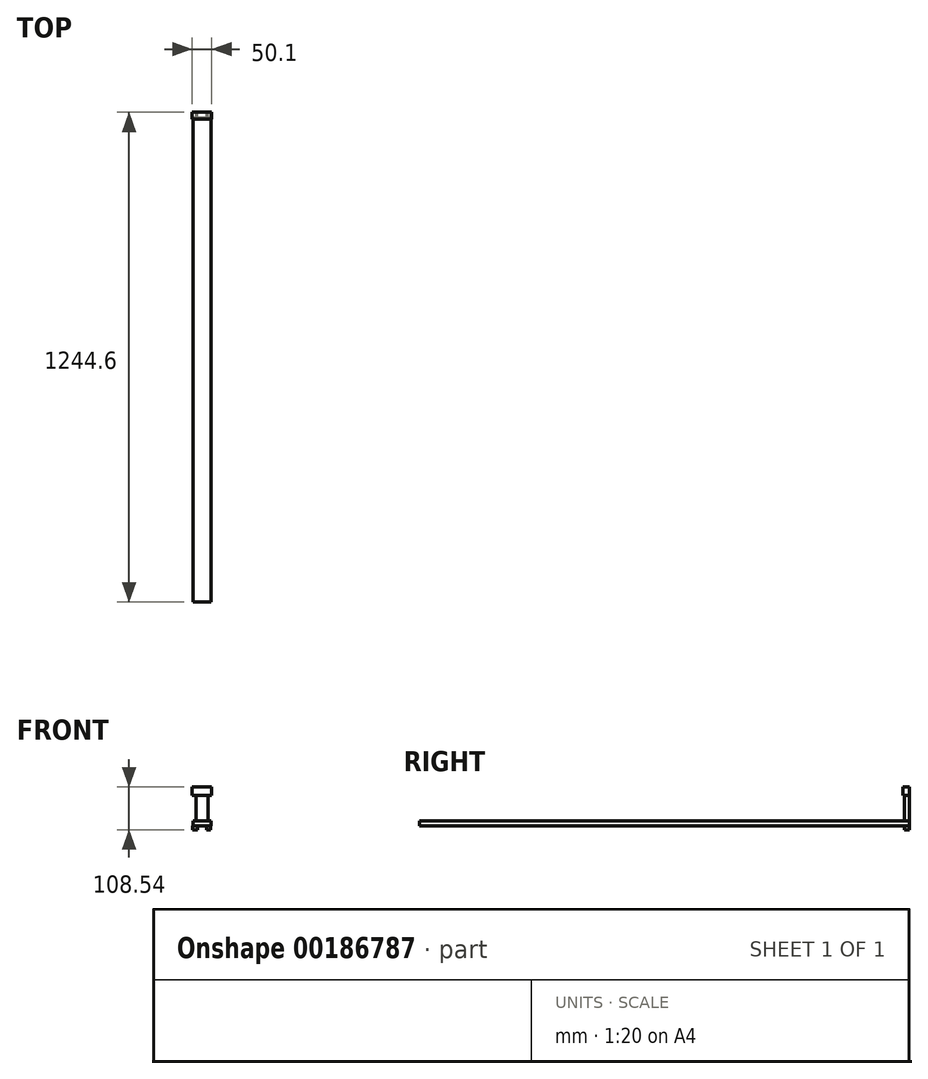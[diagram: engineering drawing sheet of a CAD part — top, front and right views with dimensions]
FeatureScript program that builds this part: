
annotation { "Feature Type Name" : "Feature", "Feature Type Description" : "" }
export const myFeature = defineFeature(function(context is Context, id is Id, definition is map)
    precondition{}
    {
        {
            var Q0;
            Q0=qCreatedBy(makeId("Front.planeOp"),FACE);
            var sketch = newSketch(context, id + "F0", { "sketchPlane" : qUnion([Q0])});
            skLineSegment(sketch, "E0.bottom", {"start": v(-11.69, 50.51) * mm, "end": v(18.65, 50.51) * mm});
            skLineSegment(sketch, "E0.top", {"start": v(-11.69, -14.33) * mm, "end": v(18.65, -14.33) * mm});
            skLineSegment(sketch, "E0.left", {"start": v(-11.69, 50.51) * mm, "end": v(-11.69, -14.33) * mm});
            skLineSegment(sketch, "E0.right", {"start": v(18.65, 50.51) * mm, "end": v(18.65, -14.33) * mm});
            skSolve(sketch);
        }
        {
            var Q0;
            Q0=qCreatedBy(makeId("Front.planeOp"),FACE);
            var sketch = newSketch(context, id + "F1", { "sketchPlane" : qUnion([Q0])});
            skLineSegment(sketch, "E1.bottom", {"start": v(-21.7, 72.22) * mm, "end": v(28.39, 72.22) * mm});
            skLineSegment(sketch, "E1.top", {"start": v(-21.7, 50.79) * mm, "end": v(28.39, 50.79) * mm});
            skLineSegment(sketch, "E1.left", {"start": v(-21.7, 72.22) * mm, "end": v(-21.7, 50.79) * mm});
            skLineSegment(sketch, "E1.right", {"start": v(28.39, 72.22) * mm, "end": v(28.39, 50.79) * mm});
            skSolve(sketch);
        }
        {
            var Q0;
            Q0=qCreatedBy(makeId("Front.planeOp"),FACE);
            var sketch = newSketch(context, id + "F2", { "sketchPlane" : qUnion([Q0])});
            skLineSegment(sketch, "E2.bottom", {"start": v(-19.48, -14.33) * mm, "end": v(26.44, -14.33) * mm});
            skLineSegment(sketch, "E2.top", {"start": v(-19.48, -26.02) * mm, "end": v(26.44, -26.02) * mm});
            skLineSegment(sketch, "E2.left", {"start": v(-19.48, -14.33) * mm, "end": v(-19.48, -26.02) * mm});
            skLineSegment(sketch, "E2.right", {"start": v(26.44, -14.33) * mm, "end": v(26.44, -26.02) * mm});
            skSolve(sketch);
        }
        {
            var Q0;
            Q0=qCreatedBy(makeId("Front.planeOp"),FACE);
            var sketch = newSketch(context, id + "F3", { "sketchPlane" : qUnion([Q0])});
            skLineSegment(sketch, "E3.bottom", {"start": v(-20.32, -26.58) * mm, "end": v(-7.51, -26.58) * mm});
            skLineSegment(sketch, "E3.top", {"start": v(-20.32, -36.32) * mm, "end": v(-7.51, -36.32) * mm});
            skLineSegment(sketch, "E3.left", {"start": v(-20.32, -26.58) * mm, "end": v(-20.32, -36.32) * mm});
            skLineSegment(sketch, "E3.right", {"start": v(-7.51, -26.58) * mm, "end": v(-7.51, -36.32) * mm});
            skSolve(sketch);
        }
        {
            var Q0;
            Q0=qCreatedBy(makeId("Front.planeOp"),FACE);
            var sketch = newSketch(context, id + "F4", { "sketchPlane" : qUnion([Q0])});
            skLineSegment(sketch, "E4.bottom", {"start": v(14.47, -26.58) * mm, "end": v(25.32, -26.58) * mm});
            skLineSegment(sketch, "E4.top", {"start": v(14.47, -36.04) * mm, "end": v(25.32, -36.04) * mm});
            skLineSegment(sketch, "E4.left", {"start": v(14.47, -26.58) * mm, "end": v(14.47, -36.04) * mm});
            skLineSegment(sketch, "E4.right", {"start": v(25.32, -26.58) * mm, "end": v(25.32, -36.04) * mm});
            skSolve(sketch);
        }
        {
            var Q0;
            Q0=makeQuery(id+"F1.imprint","IMPRINT",FACE,{"disambiguationData":[TD([[makeQuery(id+"F1.imprint","IMPRINT",EDGE,{"derivedFrom":sQuery(id+"F1.wireOp",EDGE,"E1.bottom")}),-1.0]])]});
            extrude(context, id + "F5", {"entities" : qUnion([Q0]), "depth" : 17.02 * mm});
        }
        {
            var Q0;
            Q0=makeQuery(id+"F0.imprint","IMPRINT",FACE,{"disambiguationData":[TD([[makeQuery(id+"F0.imprint","IMPRINT",EDGE,{"derivedFrom":sQuery(id+"F0.wireOp",EDGE,"E0.bottom")}),-1.0]])]});
            extrude(context, id + "F6", {"entities" : qUnion([Q0]), "depth" : 12.45 * mm});
        }
        {
            var Q0;
            Q0=makeQuery(id+"F2.imprint","IMPRINT",FACE,{"disambiguationData":[TD([[makeQuery(id+"F2.imprint","IMPRINT",EDGE,{"derivedFrom":sQuery(id+"F2.wireOp",EDGE,"E2.bottom")}),-1.0]])]});
            extrude(context, id + "F7", {"entities" : qUnion([Q0]), "operationType" : NewBodyOperationType.ADD, "depth" : 1244.6 * mm});
        }
        {
            var Q0;
            Q0=makeQuery(id+"F7.opExtrude","CAP_FACE",FACE,{"disambiguationData":[OSD([sQuery(id+"F2.wireOp",EDGE,"E2.bottom"),sQuery(id+"F2.wireOp",EDGE,"E2.top"),sQuery(id+"F2.wireOp",EDGE,"E2.left"),sQuery(id+"F2.wireOp",EDGE,"E2.right")])],"isStart":false});
            extrude(context, id + "F8", {"entities" : qUnion([Q0]), "operationType" : NewBodyOperationType.ADD, "oppositeDirection" : true, "depth" : 12.45 * mm});
        }
        {
            var Q0;
            Q0=makeQuery(id+"F4.imprint","IMPRINT",FACE,{"disambiguationData":[TD([[makeQuery(id+"F4.imprint","IMPRINT",EDGE,{"derivedFrom":sQuery(id+"F4.wireOp",EDGE,"E4.bottom")}),-1.0]])]});
            extrude(context, id + "F9", {"entities" : qUnion([Q0]), "depth" : 12.45 * mm});
        }
        {
            var Q0;
            Q0=makeQuery(id+"F3.imprint","IMPRINT",FACE,{"disambiguationData":[TD([[makeQuery(id+"F3.imprint","IMPRINT",EDGE,{"derivedFrom":sQuery(id+"F3.wireOp",EDGE,"E3.bottom")}),-1.0]])]});
            extrude(context, id + "F10", {"entities" : qUnion([Q0]), "depth" : 12.45 * mm});
        }
    });
